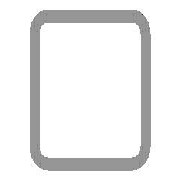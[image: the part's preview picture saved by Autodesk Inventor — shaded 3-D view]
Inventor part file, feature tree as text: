
AUTODESK INVENTOR PART (.ipt)
format: ipt  version: 2018 (Build 220112000, 112)  size: 164,864 bytes
history: native  units: mm (DEFAULTED — no unit token found)
features: sketch x6, other x4, extrude x2, hole x2, plane x1
ambient origin geometry x8: Origin, YZ Plane, XZ Plane, XY Plane, X Axis, Y Axis, Z Axis, Center Point
bodies: Solid1 (feature_tree)
feature tree (15):
  other  "Tubolare telaietto lungo 45"
  other  "Driven Length"
  other  "Piano iniziale"
  other  "Piano finale"
  extrude  "Corpo"  TaperAngle=0.0deg  [1 undecoded]
  extrude  "Estrusione2"  Depth=20.0mm
  hole  "Foro1"  [1 undecoded]
  hole  "Foro2"  [1 undecoded]
  sketch  "Schizzo"
  sketch  "Sketch3"  dims[d3=340.0mm d4=0.0mm]
  plane  "Work Plane3"
  sketch  "Sketch4"  dims[d7=4.0mm d9=20.0mm d11=20.0mm d12=2.0mm d13=-0.0mm d14=340.0mm d15=10.0mm d16=10.0mm d17=90.0deg d18=340.0mm d19=45.0deg d20=135.0deg d21=10.0mm d22=0.0mm d23=12.5mm d24=10.0mm d25=6.0mm d26=4.0mm d27=2.0mm d28=90.0deg d29=5.0mm d30=20.594885mm d31=40.0mm d32=10.0mm d33=6.0mm d34=4.0mm d35=2.0mm d36=90.0deg d37=5.0mm d38=20.594885mm]
  sketch  "Schizzo5"
  sketch  "Schizzo6"
  sketch  "Schizzo7"
note: 3 required parameter values undecoded (feature->parameter linkage not recoverable at this tier; creation-order binding heuristic only, values carry confidence <= 0.55)
